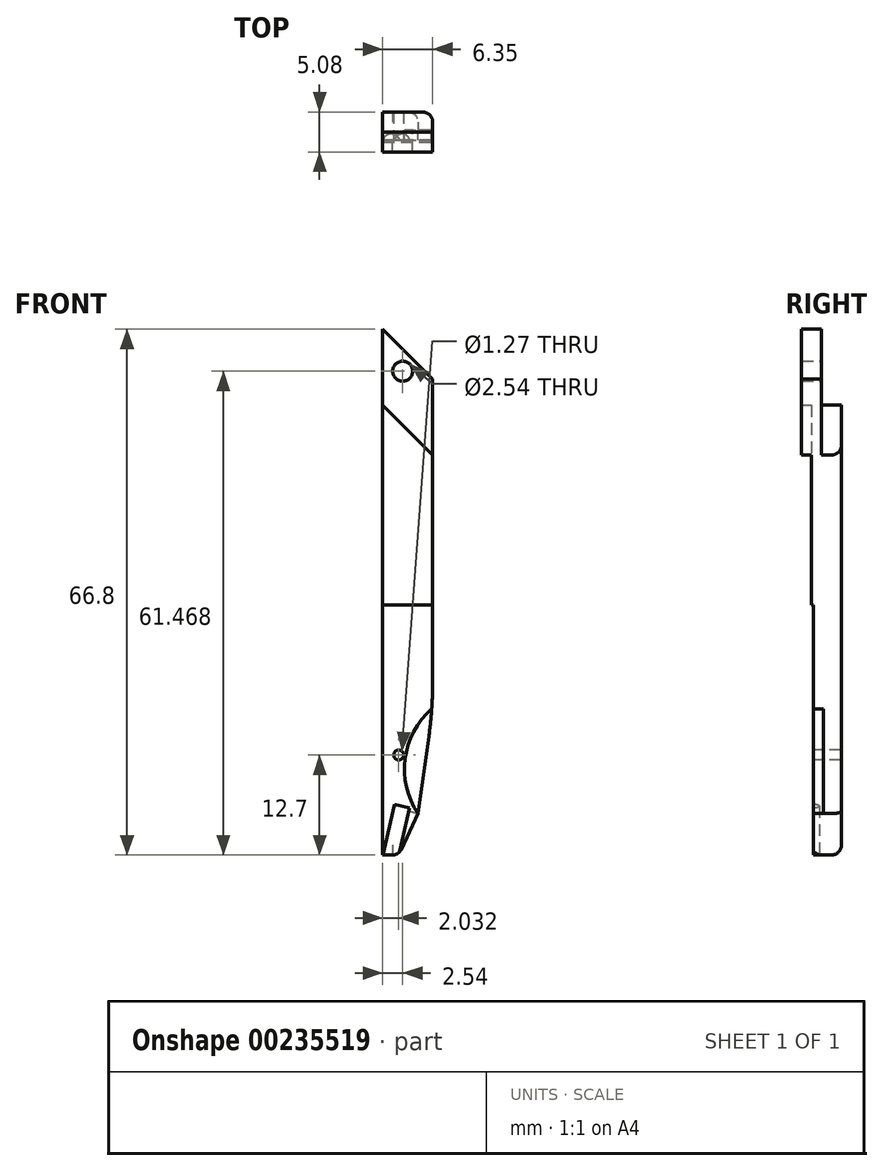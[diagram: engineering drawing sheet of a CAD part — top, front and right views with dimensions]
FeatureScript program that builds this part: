
annotation { "Feature Type Name" : "Feature", "Feature Type Description" : "" }
export const myFeature = defineFeature(function(context is Context, id is Id, definition is map)
    precondition{}
    {
        {
            var Q0;
            Q0=qCreatedBy(makeId("Front.planeOp"),FACE);
            var sketch = newSketch(context, id + "F0", { "sketchPlane" : qUnion([Q0])});
            skLineSegment(sketch, "E0", {"start": v(0, 57.15) * mm, "end": v(0, 0) * mm});
            skLineSegment(sketch, "E1", {"start": v(0, 57.15) * mm, "end": v(6.35, 50.8) * mm});
            skLineSegment(sketch, "E2", {"start": v(6.35, 50.8) * mm, "end": v(6.35, 22.1) * mm});
            skLineSegment(sketch, "E3", {"start": v(2.03, 0) * mm, "end": v(0, 0) * mm});
            skLineSegment(sketch, "E4", {"start": v(0, 57.15) * mm, "end": v(0, 66.8) * mm});
            skLineSegment(sketch, "E5", {"start": v(0, 66.8) * mm, "end": v(6.35, 60.45) * mm});
            skLineSegment(sketch, "E6", {"start": v(6.35, 60.45) * mm, "end": v(6.35, 50.8) * mm});
            skLineSegment(sketch, "E7", {"start": v(2.03, 0) * mm, "end": v(4.48, 5.25) * mm});
            skLineSegment(sketch, "E8", {"start": v(4.48, 5.25) * mm, "end": v(5.86, 15.03) * mm});
            skArc(sketch, "E9", {"start": v(6.35, 22.1) * mm, "mid": v(6.23, 18.55) * mm, "end": v(5.86, 15.03) * mm});
            skCircle(sketch, "E10", {"center": v(2.03, 12.7) * mm, "radius": 0.64 * mm});
            skCircle(sketch, "E11", {"center": v(2.54, 61.47) * mm, "radius": 1.27 * mm});
            skLineSegment(sketch, "E12", {"start": v(6.35, 50.8) * mm, "end": v(-7.6, 50.8) * mm, "construction": true});
            skLineSegment(sketch, "E13", {"start": v(2.03, 0) * mm, "end": v(2.03, 22.6) * mm, "construction": true});
            skSolve(sketch);
        }
        {
            var Q0;
            Q0=makeQuery(id+"F0.imprint","IMPRINT",FACE,{"disambiguationData":[TD([[makeQuery(id+"F0.imprint","IMPRINT",EDGE,{"derivedFrom":sQuery(id+"F0.wireOp",EDGE,"E0")}),1.0]])]});
            extrude(context, id + "F1", {"entities" : qUnion([Q0]), "oppositeDirection" : true, "depth" : 3.8 * mm});
        }
        {
            var Q0;
            Q0=makeQuery(id+"F0.imprint","IMPRINT",FACE,{"disambiguationData":[TD([[makeQuery(id+"F0.imprint","IMPRINT",EDGE,{"derivedFrom":sQuery(id+"F0.wireOp",EDGE,"E0")}),1.0]])]});
            var sketch = newSketch(context, id + "F2", { "sketchPlane" : qUnion([Q0])});
            skLineSegment(sketch, "E14", {"start": v(0, 31.75) * mm, "end": v(6.35, 31.75) * mm});
            skLineSegment(sketch, "E15.0", {"start": v(0, 31.75) * mm, "end": v(0, 0) * mm});
            skLineSegment(sketch, "E16.0", {"start": v(6.35, 31.75) * mm, "end": v(6.35, 22.1) * mm});
            skPoint(sketch, "E17.0", {"position": v(6.23, 18.55) * mm});
            skLineSegment(sketch, "E18.0", {"start": v(4.48, 5.25) * mm, "end": v(5.86, 15.03) * mm});
            skPoint(sketch, "E19.0", {"position": v(3.26, 2.63) * mm});
            skLineSegment(sketch, "E20.0", {"start": v(2.03, 0) * mm, "end": v(4.48, 5.25) * mm});
            skLineSegment(sketch, "E21.0", {"start": v(2.03, 0) * mm, "end": v(0, 0) * mm});
            skArc(sketch, "E22.0", {"start": v(6.35, 22.1) * mm, "mid": v(6.23, 18.55) * mm, "end": v(5.86, 15.03) * mm});
            skPoint(sketch, "E23.orphan", {"position": v(6.35, 50.8) * mm});
            skLineSegment(sketch, "E24.0", {"start": v(0, 57.15) * mm, "end": v(0, 0) * mm});
            skSolve(sketch);
        }
        {
            var Q0;
            {var subQ2=sQuery(id+"F2.wireOp",EDGE,"E14");Q0=makeQuery(id+"F2.imprint","IMPRINT",FACE,{"disambiguationData":[TD([[makeQuery(id+"F2.imprint","IMPRINT",EDGE,{"derivedFrom":subQ2}),-1.0]])]});}
            extrude(context, id + "F3", {"entities" : qUnion([Q0]), "operationType" : NewBodyOperationType.REMOVE, "oppositeDirection" : true, "depth" : 0.25 * mm});
        }
        {
            var Q0;
            Q0=qCreatedBy(makeId("Front.planeOp"),FACE);
            var sketch = newSketch(context, id + "F4", { "sketchPlane" : qUnion([Q0])});
            skPoint(sketch, "E25", {"position": v(4.81, 7.62) * mm});
            skLineSegment(sketch, "E26.0", {"start": v(4.81, 7.62) * mm, "end": v(5.86, 15.03) * mm});
            skPoint(sketch, "E27.orphan", {"position": v(4.48, 5.25) * mm});
            skLineSegment(sketch, "E28", {"start": v(14.69, 10) * mm, "end": v(14.69, 17.64) * mm});
            skArc(sketch, "E29", {"start": v(6.23, 18.55) * mm, "mid": v(2.85, 12.23) * mm, "end": v(4.48, 5.25) * mm});
            skArc(sketch, "E30.0", {"start": v(6.35, 22.1) * mm, "mid": v(6.23, 18.55) * mm, "end": v(5.86, 15.03) * mm});
            skLineSegment(sketch, "E31.0", {"start": v(4.48, 5.25) * mm, "end": v(5.86, 15.03) * mm});
            skLineSegment(sketch, "E32", {"start": v(6.23, 18.55) * mm, "end": v(8.32, 18.55) * mm});
            skLineSegment(sketch, "E33", {"start": v(8.32, 18.55) * mm, "end": v(6.23, 5) * mm});
            skLineSegment(sketch, "E34", {"start": v(6.23, 5) * mm, "end": v(4.48, 5.25) * mm});
            skSolve(sketch);
        }
        {
            var Q0;
            Q0 = qSketchRegion(id + "F4", true);
            extrude(context, id + "F5", {"entities" : qUnion([Q0]), "operationType" : NewBodyOperationType.REMOVE, "endBound" : BoundingType.SYMMETRIC, "depth" : 3.05 * mm});
        }
        {
            var Q0;
            Q0=qCreatedBy(makeId("Front.planeOp"),FACE);
            var sketch = newSketch(context, id + "F6", { "sketchPlane" : qUnion([Q0])});
            skLineSegment(sketch, "E35", {"start": v(3.02, 13.18) * mm, "end": v(0, 0) * mm});
            skArc(sketch, "E36.0", {"start": v(6.23, 18.55) * mm, "mid": v(2.85, 12.23) * mm, "end": v(4.48, 5.25) * mm, "construction": true});
            skLineSegment(sketch, "E37", {"start": v(0, 0) * mm, "end": v(5, -1.15) * mm, "construction": true});
            skSolve(sketch);
        }
        {
            var Q0;
            Q0 = qSketchRegion(id + "F4", true);
            extrude(context, id + "F7", {"entities" : qUnion([Q0]), "operationType" : NewBodyOperationType.REMOVE, "endBound" : BoundingType.SYMMETRIC, "depth" : 3.05 * mm});
        }
        {
            var Q0;
            Q0=sQuery(id+"F6.wireOp",EDGE,"E37");
            var Q1;
            Q1=sQuery(id+"F0.wireOp",EDGE,"E0");
            cPlane(context, id + "F8", {"entities" : qUnion([Q0, Q1]), "cplaneType" : CPlaneType.LINE_ANGLE, "offset" : 25.4 * mm, "angle" : 90 * degree, "width" : 152.4 * mm, "height" : 152.4 * mm});
        }
        {
            var Q0;
            Q0=qCreatedBy(id+"F8.planeOp",FACE);
            var sketch = newSketch(context, id + "F9", { "sketchPlane" : qUnion([Q0])});
            skCircle(sketch, "E38", {"center": v(1.02, 0) * mm, "radius": 1.02 * mm});
            skSolve(sketch);
        }
        {
            var Q0;
            Q0 = qSketchRegion(id + "F9", true);
            extrude(context, id + "F10", {"entities" : qUnion([Q0]), "operationType" : NewBodyOperationType.REMOVE, "depth" : 6.6 * mm});
        }
        {
            var Q0;
            Q0=makeQuery(id+"F0.imprint","IMPRINT",FACE,{"disambiguationData":[TD([[makeQuery(id+"F0.imprint","IMPRINT",EDGE,{"derivedFrom":sQuery(id+"F0.wireOp",EDGE,"E1")}),1.0]])]});
            extrude(context, id + "F11", {"entities" : qUnion([Q0]), "operationType" : NewBodyOperationType.ADD, "endBound" : BoundingType.SYMMETRIC, "depth" : 2.54 * mm});
        }
        {
            var Q0;
            Q0=makeQuery(id+"F1.opExtrude","CAP_EDGE",EDGE,{"disambiguationData":[OSD([sQuery(id+"F0.wireOp",EDGE,"E3")])],"isStart":false});
            var Q1;
            Q1=makeQuery(id+"FXh7RmCYcoFVjeL_1.1.F1.opExtrude","CAP_EDGE",EDGE,{"disambiguationData":[OSD([sQuery(id+"F0.wireOp",EDGE,"E3")])],"isStart":false});
            fillet(context, id + "F12", {"entities" : qUnion([Q0, Q1]), "radius" : 1.27 * mm, "tangentPropagation" : true, "allowEdgeOverflow" : false});
        }
        {
            var Q0;
            Q0=makeQuery(id+"FXh7RmCYcoFVjeL_1.1.F1.opExtrude","CAP_EDGE",EDGE,{"disambiguationData":[OSD([sQuery(id+"F0.wireOp",EDGE,"E2")])],"isStart":false});
            var Q1;
            Q1=makeQuery(id+"FXh7RmCYcoFVjeL_1.1.F1.opExtrude","CAP_EDGE",EDGE,{"disambiguationData":[OSD([sQuery(id+"F0.wireOp",EDGE,"E7")])],"isStart":false});
            var Q2;
            Q2=makeQuery(id+"F1.opExtrude","CAP_EDGE",EDGE,{"disambiguationData":[OSD([sQuery(id+"F0.wireOp",EDGE,"E7")])],"isStart":false});
            var Q3;
            Q3=makeQuery(id+"F1.opExtrude","CAP_EDGE",EDGE,{"disambiguationData":[OSD([sQuery(id+"F0.wireOp",EDGE,"E8")])],"isStart":false});
            var Q4;
            Q4=makeQuery(id+"F1.opExtrude","CAP_EDGE",EDGE,{"disambiguationData":[OSD([sQuery(id+"F0.wireOp",EDGE,"E2")])],"isStart":false});
            fillet(context, id + "F13", {"entities" : qUnion([Q0, Q1, Q2, Q3, Q4]), "radius" : 1.27 * mm, "tangentPropagation" : true, "allowEdgeOverflow" : false});
        }
    });
